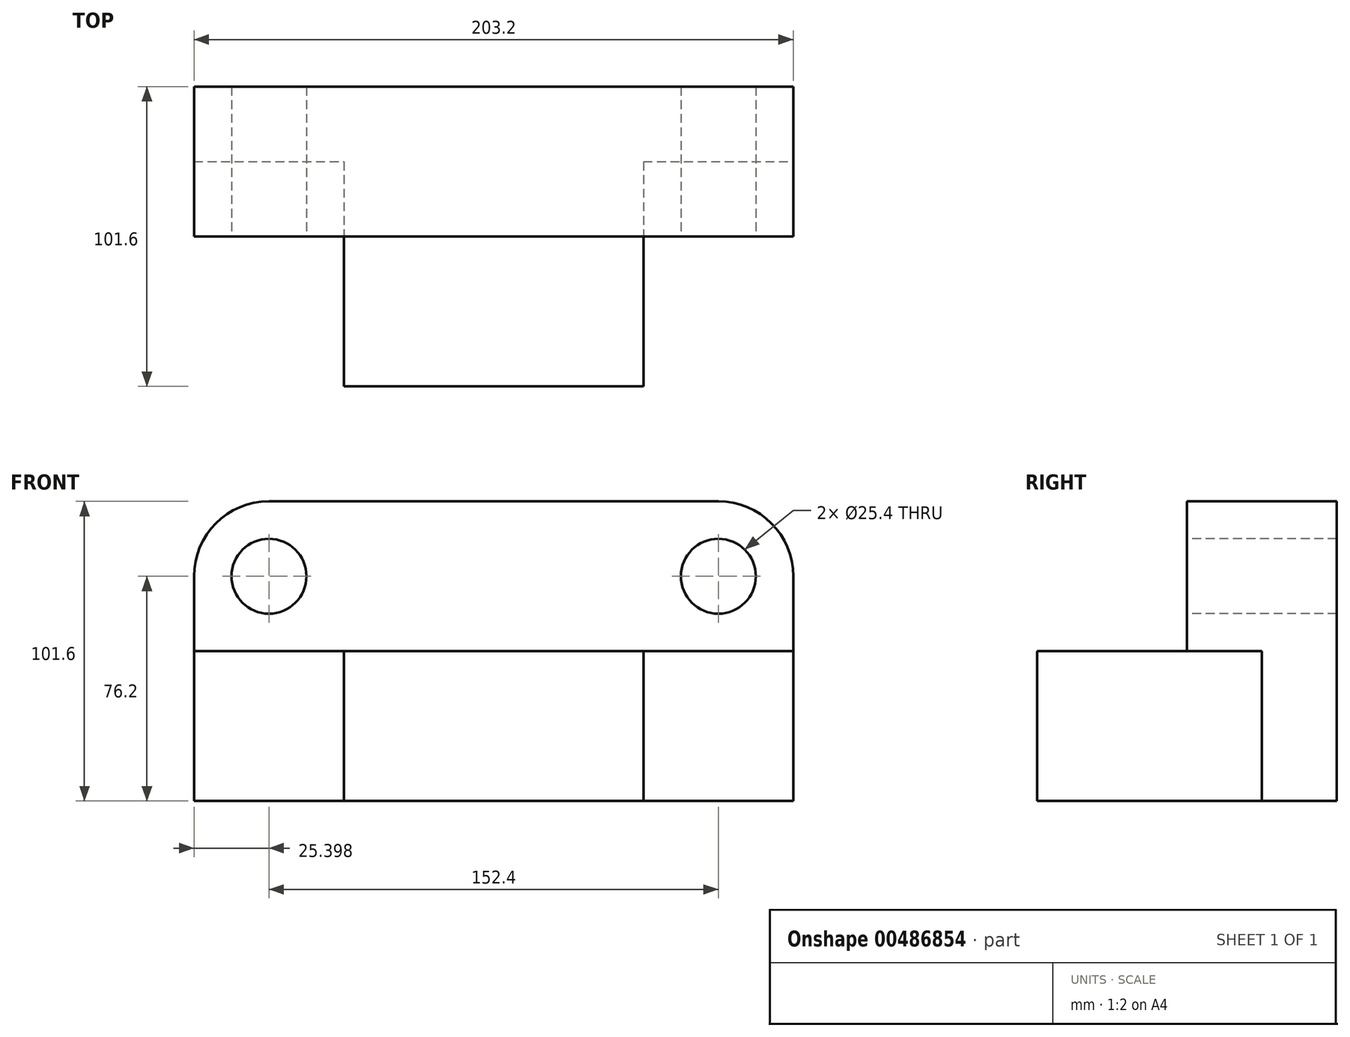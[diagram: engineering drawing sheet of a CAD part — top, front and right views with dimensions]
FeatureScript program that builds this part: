
annotation { "Feature Type Name" : "Feature", "Feature Type Description" : "" }
export const myFeature = defineFeature(function(context is Context, id is Id, definition is map)
    precondition{}
    {
        {
            var Q0;
            Q0=qCreatedBy(makeId("Top.planeOp"),FACE);
            var sketch = newSketch(context, id + "F0", { "sketchPlane" : qUnion([Q0])});
            skLineSegment(sketch, "E0.bottom", {"start": v(-63.77, 36.74) * mm, "end": v(37.83, 36.74) * mm});
            skLineSegment(sketch, "E0.top", {"start": v(-63.77, -39.46) * mm, "end": v(37.83, -39.46) * mm});
            skLineSegment(sketch, "E0.left", {"start": v(-63.77, 36.74) * mm, "end": v(-63.77, -39.46) * mm});
            skLineSegment(sketch, "E0.right", {"start": v(37.83, 36.74) * mm, "end": v(37.83, -39.46) * mm});
            skSolve(sketch);
        }
        {
            var Q0;
            Q0 = qSketchRegion(id + "F0", true);
            extrude(context, id + "F1", {"entities" : qUnion([Q0]), "depth" : 50.8 * mm});
        }
        {
            var Q0;
            Q0=makeQuery(id+"F1.opExtrude","SWEPT_FACE",FACE,{"disambiguationData":[OSD([sQuery(id+"F0.wireOp",EDGE,"E0.bottom")])]});
            var sketch = newSketch(context, id + "F2", { "sketchPlane" : qUnion([Q0])});
            skLineSegment(sketch, "E1.bottom", {"start": v(-37.83, 0) * mm, "end": v(-88.63, 0) * mm});
            skLineSegment(sketch, "E1.top", {"start": v(-37.83, 50.8) * mm, "end": v(-88.63, 50.8) * mm});
            skLineSegment(sketch, "E1.left", {"start": v(-37.83, 0) * mm, "end": v(-37.83, 50.8) * mm});
            skLineSegment(sketch, "E1.right", {"start": v(-88.63, 0) * mm, "end": v(-88.63, 50.8) * mm});
            skLineSegment(sketch, "E2.bottom", {"start": v(63.77, 0) * mm, "end": v(114.57, 0) * mm});
            skLineSegment(sketch, "E2.top", {"start": v(63.77, 50.8) * mm, "end": v(114.57, 50.8) * mm});
            skLineSegment(sketch, "E2.left", {"start": v(63.77, 0) * mm, "end": v(63.77, 50.8) * mm});
            skLineSegment(sketch, "E2.right", {"start": v(114.57, 0) * mm, "end": v(114.57, 50.8) * mm});
            skLineSegment(sketch, "E3.bottom", {"start": v(-88.63, 50.8) * mm, "end": v(114.57, 50.8) * mm});
            skLineSegment(sketch, "E3.top", {"start": v(-88.63, 0) * mm, "end": v(114.57, 0) * mm});
            skLineSegment(sketch, "E3.left", {"start": v(-88.63, 50.8) * mm, "end": v(-88.63, 0) * mm});
            skLineSegment(sketch, "E3.right", {"start": v(114.57, 50.8) * mm, "end": v(114.57, 0) * mm});
            skSolve(sketch);
        }
        {
            var Q0;
            Q0 = qSketchRegion(id + "F2", true);
            extrude(context, id + "F3", {"entities" : qUnion([Q0]), "operationType" : NewBodyOperationType.ADD, "depth" : 25.4 * mm});
        }
        {
            var Q0;
            Q0=makeQuery(id+"F3.boolean.opBoolean","MERGE",FACE,{"derivedFrom":[makeQuery(id+"F1.opExtrude","CAP_FACE",FACE,{"disambiguationData":[OSD([sQuery(id+"F0.wireOp",EDGE,"E0.bottom"),sQuery(id+"F0.wireOp",EDGE,"E0.top"),sQuery(id+"F0.wireOp",EDGE,"E0.left"),sQuery(id+"F0.wireOp",EDGE,"E0.right")])],"isStart":false}),makeQuery(id+"F3.opExtrude","SWEPT_FACE",FACE,{"disambiguationData":[OSD([sQuery(id+"F2.wireOp",EDGE,"E3.bottom")])]})]});
            var sketch = newSketch(context, id + "F4", { "sketchPlane" : qUnion([Q0])});
            skLineSegment(sketch, "E4.bottom", {"start": v(88.63, 62.14) * mm, "end": v(-114.57, 62.14) * mm});
            skLineSegment(sketch, "E4.top", {"start": v(88.63, 11.34) * mm, "end": v(-114.57, 11.34) * mm});
            skLineSegment(sketch, "E4.left", {"start": v(88.63, 62.14) * mm, "end": v(88.63, 11.34) * mm});
            skLineSegment(sketch, "E4.right", {"start": v(-114.57, 62.14) * mm, "end": v(-114.57, 11.34) * mm});
            skSolve(sketch);
        }
        {
            var Q0;
            Q0 = qSketchRegion(id + "F4", true);
            extrude(context, id + "F5", {"entities" : qUnion([Q0]), "operationType" : NewBodyOperationType.ADD, "depth" : 50.8 * mm});
        }
        {
            var Q0;
            Q0=makeQuery(id+"F5.opExtrude","CAP_EDGE",EDGE,{"disambiguationData":[OSD([sQuery(id+"F4.wireOp",EDGE,"E4.left")])],"isStart":false});
            var Q1;
            Q1=makeQuery(id+"F5.opExtrude","CAP_EDGE",EDGE,{"disambiguationData":[OSD([sQuery(id+"F4.wireOp",EDGE,"E4.right")])],"isStart":false});
            fillet(context, id + "F6", {"entities" : qUnion([Q0, Q1]), "radius" : 25.4 * mm, "tangentPropagation" : true, "allowEdgeOverflow" : false});
        }
        {
            var Q0;
            Q0=makeQuery(id+"F5.opExtrude","SWEPT_FACE",FACE,{"disambiguationData":[OSD([sQuery(id+"F4.wireOp",EDGE,"E4.top")])]});
            var sketch = newSketch(context, id + "F7", { "sketchPlane" : qUnion([Q0])});
            skCircle(sketch, "E5", {"center": v(63.23, 76.2) * mm, "radius": 12.7 * mm});
            skSolve(sketch);
        }
        {
            var Q0;
            Q0 = qSketchRegion(id + "F7", true);
            extrude(context, id + "F8", {"entities" : qUnion([Q0]), "operationType" : NewBodyOperationType.REMOVE, "oppositeDirection" : true, "depth" : 53.1 * mm});
        }
        {
            var Q0;
            Q0=makeQuery(id+"F5.opExtrude","SWEPT_FACE",FACE,{"disambiguationData":[OSD([sQuery(id+"F4.wireOp",EDGE,"E4.top")])]});
            var sketch = newSketch(context, id + "F9", { "sketchPlane" : qUnion([Q0])});
            skCircle(sketch, "E6", {"center": v(-89.17, 76.2) * mm, "radius": 12.7 * mm});
            skSolve(sketch);
        }
        {
            var Q0;
            Q0 = qSketchRegion(id + "F9", true);
            extrude(context, id + "F10", {"entities" : qUnion([Q0]), "operationType" : NewBodyOperationType.REMOVE, "oppositeDirection" : true, "depth" : 60.96 * mm});
        }
    });
